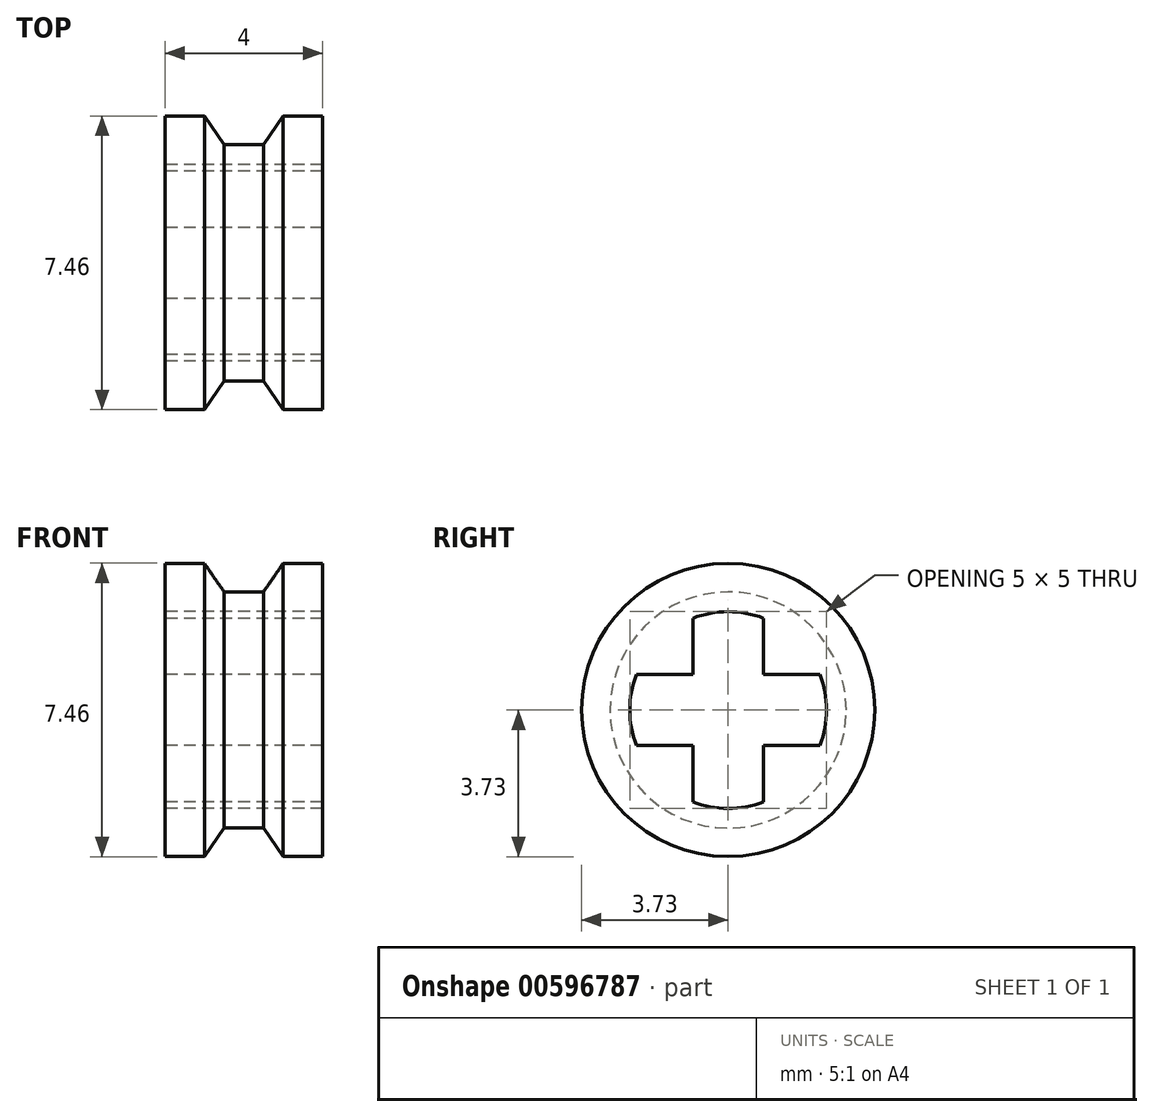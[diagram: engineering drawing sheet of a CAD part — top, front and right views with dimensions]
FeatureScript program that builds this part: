
annotation { "Feature Type Name" : "Feature", "Feature Type Description" : "" }
export const myFeature = defineFeature(function(context is Context, id is Id, definition is map)
    precondition{}
    {
        {
            var Q0;
            Q0=qCreatedBy(makeId("Front.planeOp"),FACE);
            var sketch = newSketch(context, id + "F0", { "sketchPlane" : qUnion([Q0])});
            skLineSegment(sketch, "E0.left", {"start": v(2, 3.73) * mm, "end": v(2, 0) * mm});
            skLineSegment(sketch, "E0.right", {"start": v(-2, 3.73) * mm, "end": v(-2, 0) * mm});
            skPoint(sketch, "E0.middle", {"position": v(0, 0) * mm});
            skLineSegment(sketch, "E1", {"start": v(-5.16, 0) * mm, "end": v(5.45, 0) * mm, "construction": true});
            skPoint(sketch, "E1.endSnap0", {"position": v(2, 0) * mm});
            skLineSegment(sketch, "E2", {"start": v(-2, 0) * mm, "end": v(2, 0) * mm});
            skLineSegment(sketch, "E3", {"start": v(2, 3.73) * mm, "end": v(1, 3.73) * mm});
            skLineSegment(sketch, "E4", {"start": v(-2, 3.73) * mm, "end": v(-1, 3.73) * mm});
            skLineSegment(sketch, "E5", {"start": v(0.5, 3) * mm, "end": v(1, 3.73) * mm});
            skLineSegment(sketch, "E6", {"start": v(-1, 3.73) * mm, "end": v(-0.5, 3) * mm});
            skLineSegment(sketch, "E7", {"start": v(0.5, 3) * mm, "end": v(-0.5, 3) * mm});
            skSolve(sketch);
        }
        {
            var Q0;
            Q0=makeQuery(id+"F0.imprint","IMPRINT",FACE,{"disambiguationData":[TD([[makeQuery(id+"F0.imprint","IMPRINT",EDGE,{"derivedFrom":sQuery(id+"F0.wireOp",EDGE,"E0.left")}),-1.0]])]});
            var Q1;
            Q1=sQuery(id+"F0.wireOp",EDGE,"E1");
            revolve(context, id + "F1", {"entities" : qUnion([Q0]), "axis" : qUnion([Q1]), "revolveType" : RevolveType.FULL});
        }
        {
            var Q0;
            Q0=makeQuery(id+"F1.opRevolve","SWEPT_FACE",FACE,{"disambiguationData":[OSD([sQuery(id+"F0.wireOp",EDGE,"E0.right")])]});
            var sketch = newSketch(context, id + "F2", { "sketchPlane" : qUnion([Q0])});
            skCircle(sketch, "E8", {"center": v(0, 0) * mm, "radius": 2.5 * mm});
            skLineSegment(sketch, "E9", {"start": v(0, 0) * mm, "end": v(-0.9, 0) * mm, "construction": true});
            skLineSegment(sketch, "E10", {"start": v(-0.9, 0) * mm, "end": v(0.9, 0) * mm, "construction": true});
            skLineSegment(sketch, "E11", {"start": v(0, 0) * mm, "end": v(0, 0.9) * mm, "construction": true});
            skLineSegment(sketch, "E12", {"start": v(0, 0.9) * mm, "end": v(0, -0.9) * mm, "construction": true});
            skLineSegment(sketch, "E13", {"start": v(-0.9, 2.33) * mm, "end": v(-0.9, 0.9) * mm});
            skLineSegment(sketch, "E14", {"start": v(-0.9, 0.9) * mm, "end": v(-2.33, 0.9) * mm});
            skLineSegment(sketch, "E15", {"start": v(-0.9, -2.33) * mm, "end": v(-0.9, -0.9) * mm});
            skLineSegment(sketch, "E16", {"start": v(-0.9, -0.9) * mm, "end": v(-2.33, -0.9) * mm});
            skLineSegment(sketch, "E17", {"start": v(0.9, -2.33) * mm, "end": v(0.9, -0.9) * mm});
            skLineSegment(sketch, "E18", {"start": v(0.9, -0.9) * mm, "end": v(2.33, -0.9) * mm});
            skLineSegment(sketch, "E19", {"start": v(0.9, 2.33) * mm, "end": v(0.9, 0.9) * mm});
            skLineSegment(sketch, "E20", {"start": v(0.9, 0.9) * mm, "end": v(2.33, 0.9) * mm});
            skSolve(sketch);
        }
        {
            var Q0;
            {var subQ4=sQuery(id+"F2.wireOp",EDGE,"E13");Q0=makeQuery(id+"F2.imprint","IMPRINT",FACE,{"disambiguationData":[TD([[makeQuery(id+"F2.imprint","IMPRINT",EDGE,{"derivedFrom":subQ4}),1.0]])]});}
            extrude(context, id + "F3", {"entities" : qUnion([Q0]), "operationType" : NewBodyOperationType.REMOVE, "endBound" : BoundingType.THROUGH_ALL, "oppositeDirection" : true, "depth" : 25 * mm, "offsetDistance" : 25 * mm});
        }
    });
